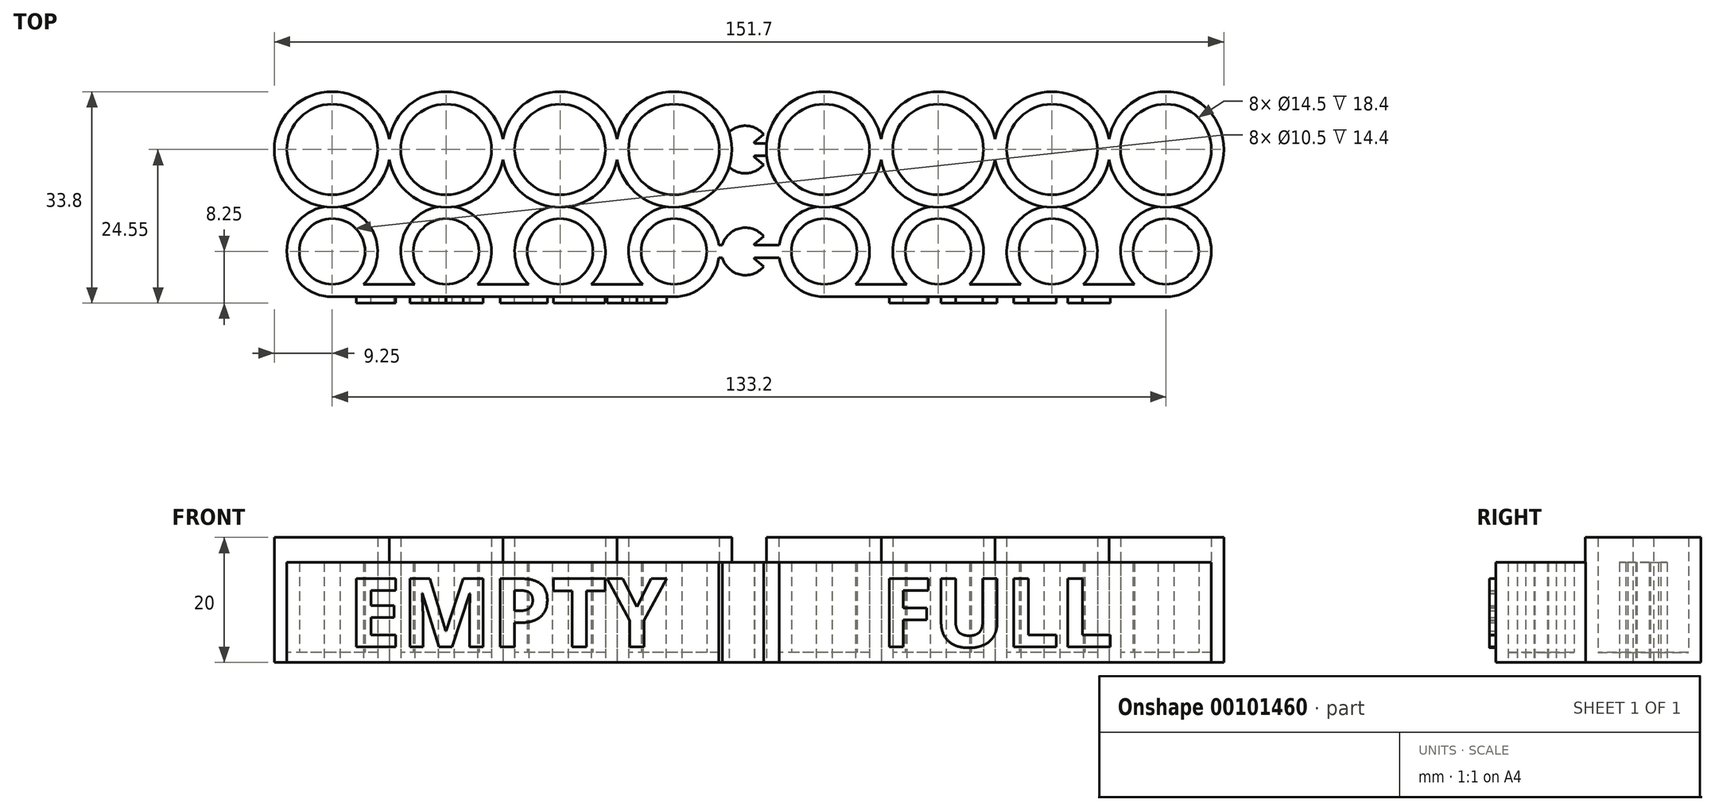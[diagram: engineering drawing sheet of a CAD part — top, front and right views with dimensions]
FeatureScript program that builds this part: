
annotation { "Feature Type Name" : "Feature", "Feature Type Description" : "" }
export const myFeature = defineFeature(function(context is Context, id is Id, definition is map)
    precondition{}
    {
        {
            var Q0;
            Q0=qCreatedBy(makeId("Top.planeOp"),FACE);
            var sketch = newSketch(context, id + "F0", { "sketchPlane" : qUnion([Q0])});
            skCircle(sketch, "E0", {"center": v(0, 0) * mm, "radius": 7.25 * mm});
            skCircle(sketch, "E1.0", {"center": v(0, 0) * mm, "radius": 9.25 * mm});
            skCircle(sketch, "E2.1.0.0", {"center": v(18.2, 0) * mm, "radius": 7.25 * mm});
            skCircle(sketch, "E2.1.0.1", {"center": v(18.2, 0) * mm, "radius": 9.25 * mm});
            skCircle(sketch, "E2.2.0.0", {"center": v(36.4, 0) * mm, "radius": 7.25 * mm});
            skCircle(sketch, "E2.2.0.1", {"center": v(36.4, 0) * mm, "radius": 9.25 * mm});
            skCircle(sketch, "E2.3.0.0", {"center": v(54.6, 0) * mm, "radius": 7.25 * mm});
            skCircle(sketch, "E2.3.0.1", {"center": v(54.6, 0) * mm, "radius": 9.25 * mm});
            skLineSegment(sketch, "E2.direction1", {"start": v(0, 0) * mm, "end": v(18.2, 0) * mm, "construction": true});
            skCircle(sketch, "E3", {"center": v(-24, 0) * mm, "radius": 7.25 * mm});
            skCircle(sketch, "E4.0", {"center": v(-24, 0) * mm, "radius": 9.25 * mm});
            skCircle(sketch, "E5.1.0.0", {"center": v(-42.2, 0) * mm, "radius": 9.25 * mm});
            skCircle(sketch, "E5.1.0.1", {"center": v(-42.2, 0) * mm, "radius": 7.25 * mm});
            skCircle(sketch, "E5.2.0.0", {"center": v(-60.4, 0) * mm, "radius": 9.25 * mm});
            skCircle(sketch, "E5.2.0.1", {"center": v(-60.4, 0) * mm, "radius": 7.25 * mm});
            skLineSegment(sketch, "E5.direction1", {"start": v(-24, 0) * mm, "end": v(-42.2, 0) * mm, "construction": true});
            skCircle(sketch, "E6.0.3.0", {"center": v(-78.6, 0) * mm, "radius": 9.25 * mm});
            skCircle(sketch, "E6.2.3.0", {"center": v(-78.6, 0) * mm, "radius": 7.25 * mm});
            skCircle(sketch, "E7", {"center": v(0, -16.3) * mm, "radius": 5.25 * mm});
            skCircle(sketch, "E8.0", {"center": v(0, -16.3) * mm, "radius": 7.25 * mm});
            skCircle(sketch, "E9.1.0.0", {"center": v(18.2, -16.3) * mm, "radius": 7.25 * mm});
            skCircle(sketch, "E9.1.0.1", {"center": v(18.2, -16.3) * mm, "radius": 5.25 * mm});
            skCircle(sketch, "E9.2.0.0", {"center": v(36.4, -16.3) * mm, "radius": 7.25 * mm});
            skCircle(sketch, "E9.2.0.1", {"center": v(36.4, -16.3) * mm, "radius": 5.25 * mm});
            skCircle(sketch, "E9.3.0.0", {"center": v(54.6, -16.3) * mm, "radius": 7.25 * mm});
            skCircle(sketch, "E9.3.0.1", {"center": v(54.6, -16.3) * mm, "radius": 5.25 * mm});
            skLineSegment(sketch, "E9.direction1", {"start": v(0, -16.3) * mm, "end": v(18.2, -16.3) * mm, "construction": true});
            skCircle(sketch, "E10", {"center": v(-24, -16.3) * mm, "radius": 5.25 * mm});
            skCircle(sketch, "E11.0", {"center": v(-24, -16.3) * mm, "radius": 7.25 * mm});
            skCircle(sketch, "E12.1.0.0", {"center": v(-42.2, -16.3) * mm, "radius": 7.25 * mm});
            skCircle(sketch, "E12.1.0.1", {"center": v(-42.2, -16.3) * mm, "radius": 5.25 * mm});
            skCircle(sketch, "E12.2.0.0", {"center": v(-60.4, -16.3) * mm, "radius": 7.25 * mm});
            skCircle(sketch, "E12.2.0.1", {"center": v(-60.4, -16.3) * mm, "radius": 5.25 * mm});
            skCircle(sketch, "E12.3.0.0", {"center": v(-78.6, -16.3) * mm, "radius": 7.25 * mm});
            skCircle(sketch, "E12.3.0.1", {"center": v(-78.6, -16.3) * mm, "radius": 5.25 * mm});
            skLineSegment(sketch, "E12.direction1", {"start": v(-24, -16.3) * mm, "end": v(-42.2, -16.3) * mm, "construction": true});
            skLineSegment(sketch, "E13", {"start": v(-9.2, 1) * mm, "end": v(-14.8, 1) * mm});
            skLineSegment(sketch, "E14.MirrorCS", {"start": v(-9.2, -1) * mm, "end": v(-14.8, -1) * mm});
            skLineSegment(sketch, "E15", {"start": v(-7.18, -15.3) * mm, "end": v(-16.82, -15.3) * mm});
            skLineSegment(sketch, "E16.MirrorCS", {"start": v(-7.18, -17.3) * mm, "end": v(-16.82, -17.3) * mm});
            skLineSegment(sketch, "E17", {"start": v(-78.6, -23.55) * mm, "end": v(-24, -23.55) * mm});
            skLineSegment(sketch, "E18", {"start": v(49.6, -21.55) * mm, "end": v(41.4, -21.55) * mm});
            skLineSegment(sketch, "E19.trimOffspring", {"start": v(0, -23.55) * mm, "end": v(54.6, -23.55) * mm});
            skPoint(sketch, "E20.orphan", {"position": v(-78.6, -21.55) * mm});
            skLineSegment(sketch, "E21.trimOffspring", {"start": v(-65.4, -21.55) * mm, "end": v(-73.6, -21.55) * mm});
            skLineSegment(sketch, "E22.trimOffspring", {"start": v(-47.2, -21.55) * mm, "end": v(-55.4, -21.55) * mm});
            skLineSegment(sketch, "E23.trimOffspring", {"start": v(-29, -21.55) * mm, "end": v(-37.2, -21.55) * mm});
            skLineSegment(sketch, "E24.trimOffspring", {"start": v(13.2, -21.55) * mm, "end": v(5, -21.55) * mm});
            skLineSegment(sketch, "E25.trimOffspring", {"start": v(31.4, -21.55) * mm, "end": v(23.2, -21.55) * mm});
            skPoint(sketch, "E26.orphan", {"position": v(54.6, -21.55) * mm});
            skCircle(sketch, "E27", {"center": v(-12.6, 0) * mm, "radius": 1.8 * mm});
            skCircle(sketch, "E28.0", {"center": v(-12.6, 0) * mm, "radius": 3.8 * mm});
            skLineSegment(sketch, "E29", {"start": v(-12.6, 0) * mm, "end": v(-9.69, 2.44) * mm});
            skLineSegment(sketch, "E30", {"start": v(-12.6, 0) * mm, "end": v(-9.69, -2.44) * mm});
            skCircle(sketch, "E31", {"center": v(-12.6, -16.3) * mm, "radius": 1.8 * mm});
            skCircle(sketch, "E32.0", {"center": v(-12.6, -16.3) * mm, "radius": 3.8 * mm});
            skLineSegment(sketch, "E33", {"start": v(-12.6, -16.3) * mm, "end": v(-9.69, -13.86) * mm});
            skLineSegment(sketch, "E34", {"start": v(-12.6, -16.3) * mm, "end": v(-9.69, -18.74) * mm});
            skSolve(sketch);
        }
        {
            var Q0;
            Q0=makeQuery(id+"F0.imprint","IMPRINT",FACE,{"disambiguationData":[TD([[makeQuery(id+"F0.imprint","IMPRINT",EDGE,{"derivedFrom":sQuery(id+"F0.wireOp",EDGE,"E6.2.3.0")}),-1.0]])]});
            var Q1;
            Q1=makeQuery(id+"F0.imprint","IMPRINT",FACE,{"disambiguationData":[TD([[makeQuery(id+"F0.imprint","IMPRINT",EDGE,{"derivedFrom":sQuery(id+"F0.wireOp",EDGE,"E5.2.0.1")}),-1.0]])]});
            var Q2;
            Q2=makeQuery(id+"F0.imprint","IMPRINT",FACE,{"disambiguationData":[TD([[makeQuery(id+"F0.imprint","IMPRINT",EDGE,{"derivedFrom":sQuery(id+"F0.wireOp",EDGE,"E5.1.0.1")}),-1.0]])]});
            var Q3;
            {var subQ3=sQuery(id+"F0.wireOp",EDGE,"E28.0");var subQ6=sQuery(id+"F0.wireOp",EDGE,"E3");var subQ7=makeQuery(id+"F0.imprint","INTERSECT",VERTEX,{"disambiguationData":[OD(0.0)],"derivedFrom":[subQ6,subQ3]});Q3=makeQuery(id+"F0.imprint","IMPRINT",FACE,{"disambiguationData":[TD([[makeQuery(id+"F0.imprint","IMPRINT",EDGE,{"disambiguationData":[TD([[subQ7,-1.0]])],"derivedFrom":subQ6}),-1.0]])]});}
            var Q4;
            {var subQ2=sQuery(id+"F0.wireOp",EDGE,"E28.0");var subQ9=sQuery(id+"F0.wireOp",EDGE,"E3");var subQ10=makeQuery(id+"F0.imprint","INTERSECT",VERTEX,{"disambiguationData":[OD(0.0)],"derivedFrom":[subQ9,subQ2]});Q4=makeQuery(id+"F0.imprint","IMPRINT",FACE,{"disambiguationData":[TD([[makeQuery(id+"F0.imprint","IMPRINT",EDGE,{"disambiguationData":[TD([[subQ10,1.0]])],"derivedFrom":subQ9}),-1.0]])]});}
            var Q5;
            {var subQ0=sQuery(id+"F0.wireOp",EDGE,"E6.0.3.0");var subQ1=sQuery(id+"F0.wireOp",EDGE,"E5.2.0.0");var subQ2=makeQuery(id+"F0.imprint","INTERSECT",VERTEX,{"disambiguationData":[OD(0.0)],"derivedFrom":[subQ1,subQ0]});Q5=makeQuery(id+"F0.imprint","IMPRINT",FACE,{"disambiguationData":[TD([[makeQuery(id+"F0.imprint","IMPRINT",EDGE,{"disambiguationData":[TD([[subQ2,-1.0]])],"derivedFrom":subQ1}),1.0]])]});}
            var Q6;
            {var subQ0=sQuery(id+"F0.wireOp",EDGE,"E5.2.0.0");var subQ1=sQuery(id+"F0.wireOp",EDGE,"E5.1.0.0");var subQ2=makeQuery(id+"F0.imprint","INTERSECT",VERTEX,{"disambiguationData":[OD(0.0)],"derivedFrom":[subQ1,subQ0]});Q6=makeQuery(id+"F0.imprint","IMPRINT",FACE,{"disambiguationData":[TD([[makeQuery(id+"F0.imprint","IMPRINT",EDGE,{"disambiguationData":[TD([[subQ2,-1.0]])],"derivedFrom":subQ1}),1.0]])]});}
            var Q7;
            {var subQ0=sQuery(id+"F0.wireOp",EDGE,"E5.1.0.0");var subQ1=sQuery(id+"F0.wireOp",EDGE,"E4.0");var subQ2=makeQuery(id+"F0.imprint","INTERSECT",VERTEX,{"disambiguationData":[OD(0.0)],"derivedFrom":[subQ1,subQ0]});Q7=makeQuery(id+"F0.imprint","IMPRINT",FACE,{"disambiguationData":[TD([[makeQuery(id+"F0.imprint","IMPRINT",EDGE,{"disambiguationData":[TD([[subQ2,-1.0]])],"derivedFrom":subQ1}),1.0]])]});}
            var Q8;
            {var subQ0=sQuery(id+"F0.wireOp",EDGE,"E11.0");var subQ1=sQuery(id+"F0.wireOp",EDGE,"E4.0");var subQ2=makeQuery(id+"F0.imprint","INTERSECT",VERTEX,{"disambiguationData":[OD(0.0)],"derivedFrom":[subQ1,subQ0]});Q8=makeQuery(id+"F0.imprint","IMPRINT",FACE,{"disambiguationData":[TD([[makeQuery(id+"F0.imprint","IMPRINT",EDGE,{"disambiguationData":[TD([[subQ2,-1.0]])],"derivedFrom":subQ1}),1.0]])]});}
            var Q9;
            {var subQ0=sQuery(id+"F0.wireOp",EDGE,"E12.1.0.0");var subQ1=sQuery(id+"F0.wireOp",EDGE,"E5.1.0.0");var subQ2=makeQuery(id+"F0.imprint","INTERSECT",VERTEX,{"disambiguationData":[OD(0.0)],"derivedFrom":[subQ1,subQ0]});Q9=makeQuery(id+"F0.imprint","IMPRINT",FACE,{"disambiguationData":[TD([[makeQuery(id+"F0.imprint","IMPRINT",EDGE,{"disambiguationData":[TD([[subQ2,-1.0]])],"derivedFrom":subQ1}),1.0]])]});}
            var Q10;
            {var subQ0=sQuery(id+"F0.wireOp",EDGE,"E12.2.0.0");var subQ1=sQuery(id+"F0.wireOp",EDGE,"E5.2.0.0");var subQ2=makeQuery(id+"F0.imprint","INTERSECT",VERTEX,{"disambiguationData":[OD(0.0)],"derivedFrom":[subQ1,subQ0]});Q10=makeQuery(id+"F0.imprint","IMPRINT",FACE,{"disambiguationData":[TD([[makeQuery(id+"F0.imprint","IMPRINT",EDGE,{"disambiguationData":[TD([[subQ2,-1.0]])],"derivedFrom":subQ1}),1.0]])]});}
            var Q11;
            {var subQ0=sQuery(id+"F0.wireOp",EDGE,"E12.3.0.0");var subQ1=sQuery(id+"F0.wireOp",EDGE,"E6.0.3.0");var subQ2=makeQuery(id+"F0.imprint","INTERSECT",VERTEX,{"disambiguationData":[OD(0.0)],"derivedFrom":[subQ1,subQ0]});Q11=makeQuery(id+"F0.imprint","IMPRINT",FACE,{"disambiguationData":[TD([[makeQuery(id+"F0.imprint","IMPRINT",EDGE,{"disambiguationData":[TD([[subQ2,-1.0]])],"derivedFrom":subQ1}),1.0]])]});}
            var Q12;
            {var subQ0=sQuery(id+"F0.wireOp",EDGE,"E27");var subQ1=sQuery(id+"F0.wireOp",EDGE,"E4.0");var subQ2=makeQuery(id+"F0.imprint","INTERSECT",VERTEX,{"disambiguationData":[OD(0.0)],"derivedFrom":[subQ1,subQ0]});Q12=makeQuery(id+"F0.imprint","IMPRINT",FACE,{"disambiguationData":[TD([[makeQuery(id+"F0.imprint","IMPRINT",EDGE,{"disambiguationData":[TD([[subQ2,1.0]])],"derivedFrom":subQ1}),1.0]])]});}
            var Q13;
            {var subQ0=sQuery(id+"F0.wireOp",EDGE,"E4.0");var subQ1=makeQuery(id+"F0.imprint","INTERSECT",VERTEX,{"derivedFrom":[subQ0,sQuery(id+"F0.wireOp",EDGE,"E13")]});Q13=makeQuery(id+"F0.imprint","IMPRINT",FACE,{"disambiguationData":[TD([[makeQuery(id+"F0.imprint","IMPRINT",EDGE,{"disambiguationData":[TD([[subQ1,-1.0]])],"derivedFrom":subQ0}),1.0]])]});}
            extrude(context, id + "F1", {"entities" : qUnion([Q0, Q1, Q2, Q3, Q4, Q5, Q6, Q7, Q8, Q9, Q10, Q11, Q12, Q13]), "depth" : 20 * mm});
        }
        {
            var Q0;
            {var subQ0=sQuery(id+"F0.wireOp",EDGE,"E15");var subQ1=sQuery(id+"F0.wireOp",EDGE,"E11.0");var subQ2=makeQuery(id+"F0.imprint","INTERSECT",VERTEX,{"derivedFrom":[subQ1,subQ0]});Q0=makeQuery(id+"F0.imprint","IMPRINT",FACE,{"disambiguationData":[TD([[makeQuery(id+"F0.imprint","IMPRINT",EDGE,{"disambiguationData":[TD([[subQ2,1.0]])],"derivedFrom":subQ1}),-1.0]])]});}
            var Q1;
            {var subQ0=sQuery(id+"F0.wireOp",EDGE,"E31");var subQ1=sQuery(id+"F0.wireOp",EDGE,"E15");var subQ2=makeQuery(id+"F0.imprint","INTERSECT",VERTEX,{"disambiguationData":[OD(1.0)],"derivedFrom":[subQ1,subQ0]});Q1=makeQuery(id+"F0.imprint","IMPRINT",FACE,{"disambiguationData":[TD([[makeQuery(id+"F0.imprint","IMPRINT",EDGE,{"disambiguationData":[TD([[subQ2,-1.0]])],"derivedFrom":subQ1}),1.0]])]});}
            var Q2;
            Q2=makeQuery(id+"F0.imprint","IMPRINT",FACE,{"disambiguationData":[TD([[makeQuery(id+"F0.imprint","IMPRINT",EDGE,{"derivedFrom":sQuery(id+"F0.wireOp",EDGE,"E12.3.0.1")}),-1.0]])]});
            var Q3;
            {var subQ0=sQuery(id+"F0.wireOp",EDGE,"E21.trimOffspring");Q3=makeQuery(id+"F0.imprint","IMPRINT",FACE,{"disambiguationData":[TD([[makeQuery(id+"F0.imprint","IMPRINT",EDGE,{"derivedFrom":subQ0}),1.0]])]});}
            var Q4;
            Q4=makeQuery(id+"F0.imprint","IMPRINT",FACE,{"disambiguationData":[TD([[makeQuery(id+"F0.imprint","IMPRINT",EDGE,{"derivedFrom":sQuery(id+"F0.wireOp",EDGE,"E12.2.0.1")}),-1.0]])]});
            var Q5;
            {var subQ0=sQuery(id+"F0.wireOp",EDGE,"E22.trimOffspring");Q5=makeQuery(id+"F0.imprint","IMPRINT",FACE,{"disambiguationData":[TD([[makeQuery(id+"F0.imprint","IMPRINT",EDGE,{"derivedFrom":subQ0}),1.0]])]});}
            var Q6;
            Q6=makeQuery(id+"F0.imprint","IMPRINT",FACE,{"disambiguationData":[TD([[makeQuery(id+"F0.imprint","IMPRINT",EDGE,{"derivedFrom":sQuery(id+"F0.wireOp",EDGE,"E12.1.0.1")}),-1.0]])]});
            var Q7;
            {var subQ3=sQuery(id+"F0.wireOp",EDGE,"E23.trimOffspring");Q7=makeQuery(id+"F0.imprint","IMPRINT",FACE,{"disambiguationData":[TD([[makeQuery(id+"F0.imprint","IMPRINT",EDGE,{"derivedFrom":subQ3}),1.0]])]});}
            var Q8;
            Q8=makeQuery(id+"F0.imprint","IMPRINT",FACE,{"disambiguationData":[TD([[makeQuery(id+"F0.imprint","IMPRINT",EDGE,{"derivedFrom":sQuery(id+"F0.wireOp",EDGE,"E10")}),-1.0]])]});
            var Q9;
            {var subQ3=sQuery(id+"F0.wireOp",EDGE,"E4.0");var subQ7=sQuery(id+"F0.wireOp",EDGE,"E13");var subQ9=makeQuery(id+"F0.imprint","INTERSECT",VERTEX,{"derivedFrom":[subQ3,subQ7]});Q9=makeQuery(id+"F0.imprint","IMPRINT",FACE,{"disambiguationData":[TD([[makeQuery(id+"F0.imprint","IMPRINT",EDGE,{"disambiguationData":[TD([[subQ9,-1.0]])],"derivedFrom":subQ3}),-1.0]])]});}
            var Q10;
            {var subQ0=sQuery(id+"F0.wireOp",EDGE,"E13");var subQ1=sQuery(id+"F0.wireOp",EDGE,"E4.0");var subQ2=makeQuery(id+"F0.imprint","INTERSECT",VERTEX,{"derivedFrom":[subQ1,subQ0]});Q10=makeQuery(id+"F0.imprint","IMPRINT",FACE,{"disambiguationData":[TD([[makeQuery(id+"F0.imprint","IMPRINT",EDGE,{"disambiguationData":[TD([[subQ2,1.0]])],"derivedFrom":subQ1}),-1.0]])]});}
            var Q11;
            {var subQ0=sQuery(id+"F0.wireOp",EDGE,"E13");var subQ1=sQuery(id+"F0.wireOp",EDGE,"E4.0");var subQ2=makeQuery(id+"F0.imprint","INTERSECT",VERTEX,{"derivedFrom":[subQ1,subQ0]});Q11=makeQuery(id+"F0.imprint","IMPRINT",FACE,{"disambiguationData":[TD([[makeQuery(id+"F0.imprint","IMPRINT",EDGE,{"disambiguationData":[TD([[subQ2,1.0]])],"derivedFrom":subQ1}),-1.0]])]});}
            var Q12;
            {var subQ3=sQuery(id+"F0.wireOp",EDGE,"E4.0");var subQ6=sQuery(id+"F0.wireOp",EDGE,"E14.MirrorCS");var subQ9=makeQuery(id+"F0.imprint","INTERSECT",VERTEX,{"derivedFrom":[subQ3,subQ6]});Q12=makeQuery(id+"F0.imprint","IMPRINT",FACE,{"disambiguationData":[TD([[makeQuery(id+"F0.imprint","IMPRINT",EDGE,{"disambiguationData":[TD([[subQ9,1.0]])],"derivedFrom":subQ3}),-1.0]])]});}
            var Q13;
            {var subQ0=sQuery(id+"F0.wireOp",EDGE,"E31");var subQ1=sQuery(id+"F0.wireOp",EDGE,"E15");var subQ2=makeQuery(id+"F0.imprint","INTERSECT",VERTEX,{"disambiguationData":[OD(1.0)],"derivedFrom":[subQ1,subQ0]});Q13=makeQuery(id+"F0.imprint","IMPRINT",FACE,{"disambiguationData":[TD([[makeQuery(id+"F0.imprint","IMPRINT",EDGE,{"disambiguationData":[TD([[subQ2,-1.0]])],"derivedFrom":subQ1}),-1.0]])]});}
            var Q14;
            {var subQ0=sQuery(id+"F0.wireOp",EDGE,"E15");var subQ1=sQuery(id+"F0.wireOp",EDGE,"E11.0");var subQ2=makeQuery(id+"F0.imprint","INTERSECT",VERTEX,{"derivedFrom":[subQ1,subQ0]});Q14=makeQuery(id+"F0.imprint","IMPRINT",FACE,{"disambiguationData":[TD([[makeQuery(id+"F0.imprint","IMPRINT",EDGE,{"disambiguationData":[TD([[subQ2,1.0]])],"derivedFrom":subQ1}),-1.0]])]});}
            var Q15;
            {var subQ0=sQuery(id+"F0.wireOp",EDGE,"E32.0");var subQ1=sQuery(id+"F0.wireOp",EDGE,"E16.MirrorCS");var subQ2=makeQuery(id+"F0.imprint","INTERSECT",VERTEX,{"disambiguationData":[OD(1.0)],"derivedFrom":[subQ1,subQ0]});Q15=makeQuery(id+"F0.imprint","IMPRINT",FACE,{"disambiguationData":[TD([[makeQuery(id+"F0.imprint","IMPRINT",EDGE,{"disambiguationData":[TD([[subQ2,1.0]])],"derivedFrom":subQ1}),1.0]])]});}
            var Q16;
            Q16=makeQuery(id+"F0.imprint","IMPRINT",FACE,{"disambiguationData":[TD([[makeQuery(id+"F0.imprint","IMPRINT",EDGE,{"derivedFrom":sQuery(id+"F0.wireOp",EDGE,"E10")}),-1.0]])]});
            extrude(context, id + "F2", {"entities" : qUnion([Q0, Q1, Q2, Q3, Q4, Q5, Q6, Q7, Q8, Q9, Q10, Q11, Q12, Q13, Q14, Q15, Q16]), "operationType" : NewBodyOperationType.ADD, "depth" : 16 * mm});
        }
        {
            var Q0;
            Q0=makeQuery(id+"F0.imprint","IMPRINT",FACE,{"disambiguationData":[TD([[makeQuery(id+"F0.imprint","IMPRINT",EDGE,{"derivedFrom":sQuery(id+"F0.wireOp",EDGE,"E5.1.0.1")}),1.0]])]});
            var Q1;
            Q1=makeQuery(id+"F0.imprint","IMPRINT",FACE,{"disambiguationData":[TD([[makeQuery(id+"F0.imprint","IMPRINT",EDGE,{"derivedFrom":sQuery(id+"F0.wireOp",EDGE,"E3")}),1.0]])]});
            var Q2;
            Q2=makeQuery(id+"F0.imprint","IMPRINT",FACE,{"disambiguationData":[TD([[makeQuery(id+"F0.imprint","IMPRINT",EDGE,{"derivedFrom":sQuery(id+"F0.wireOp",EDGE,"E5.2.0.1")}),1.0]])]});
            var Q3;
            Q3=makeQuery(id+"F0.imprint","IMPRINT",FACE,{"disambiguationData":[TD([[makeQuery(id+"F0.imprint","IMPRINT",EDGE,{"derivedFrom":sQuery(id+"F0.wireOp",EDGE,"E6.2.3.0")}),1.0]])]});
            var Q4;
            Q4=makeQuery(id+"F0.imprint","IMPRINT",FACE,{"disambiguationData":[TD([[makeQuery(id+"F0.imprint","IMPRINT",EDGE,{"derivedFrom":sQuery(id+"F0.wireOp",EDGE,"E10")}),1.0]])]});
            var Q5;
            Q5=makeQuery(id+"F0.imprint","IMPRINT",FACE,{"disambiguationData":[TD([[makeQuery(id+"F0.imprint","IMPRINT",EDGE,{"derivedFrom":sQuery(id+"F0.wireOp",EDGE,"E12.1.0.1")}),1.0]])]});
            var Q6;
            Q6=makeQuery(id+"F0.imprint","IMPRINT",FACE,{"disambiguationData":[TD([[makeQuery(id+"F0.imprint","IMPRINT",EDGE,{"derivedFrom":sQuery(id+"F0.wireOp",EDGE,"E12.2.0.1")}),1.0]])]});
            var Q7;
            Q7=makeQuery(id+"F0.imprint","IMPRINT",FACE,{"disambiguationData":[TD([[makeQuery(id+"F0.imprint","IMPRINT",EDGE,{"derivedFrom":sQuery(id+"F0.wireOp",EDGE,"E12.3.0.1")}),1.0]])]});
            extrude(context, id + "F3", {"entities" : qUnion([Q0, Q1, Q2, Q3, Q4, Q5, Q6, Q7]), "operationType" : NewBodyOperationType.ADD, "depth" : 1.6 * mm});
        }
        {
            var Q0;
            Q0=makeQuery(id+"F2.opExtrude","SWEPT_FACE",FACE,{"disambiguationData":[OSD([sQuery(id+"F0.wireOp",EDGE,"E17")])]});
            var sketch = newSketch(context, id + "F4", { "sketchPlane" : qUnion([Q0])});
            skText(sketch, "E35", { "text": "EMPTY", "fontName": "OpenSans-Bold.ttf"});
            const initialGuessF4  = {"E35": [-0.0761, 0.0025, 1, 0, 0.011]};
            skSetInitialGuess(sketch, initialGuessF4);
            skSolve(sketch);
        }
        {
            var Q0;
            Q0=makeQuery(id+"F4.imprint","IMPRINT",FACE,{"disambiguationData":[TD([[makeQuery(id+"F4.imprint","IMPRINT",EDGE,{"derivedFrom":sQuery(id+"F4.wireOp",EDGE,"E35.sketch_text.stroke-0")}),-1.0]])]});
            var Q1;
            Q1=makeQuery(id+"F4.imprint","IMPRINT",FACE,{"disambiguationData":[TD([[makeQuery(id+"F4.imprint","IMPRINT",EDGE,{"derivedFrom":sQuery(id+"F4.wireOp",EDGE,"E35.sketch_text.stroke-12")}),-1.0]])]});
            var Q2;
            Q2=makeQuery(id+"F4.imprint","IMPRINT",FACE,{"disambiguationData":[TD([[makeQuery(id+"F4.imprint","IMPRINT",EDGE,{"derivedFrom":sQuery(id+"F4.wireOp",EDGE,"E35.sketch_text.stroke-31")}),-1.0]])]});
            var Q3;
            Q3=makeQuery(id+"F4.imprint","IMPRINT",FACE,{"disambiguationData":[TD([[makeQuery(id+"F4.imprint","IMPRINT",EDGE,{"derivedFrom":sQuery(id+"F4.wireOp",EDGE,"E35.sketch_text.stroke-47")}),-1.0]])]});
            var Q4;
            Q4=makeQuery(id+"F4.imprint","IMPRINT",FACE,{"disambiguationData":[TD([[makeQuery(id+"F4.imprint","IMPRINT",EDGE,{"derivedFrom":sQuery(id+"F4.wireOp",EDGE,"E35.sketch_text.stroke-55")}),-1.0]])]});
            extrude(context, id + "F5", {"entities" : qUnion([Q0, Q1, Q2, Q3, Q4]), "operationType" : NewBodyOperationType.ADD, "depth" : 1 * mm});
        }
        {
            var Q0;
            Q0=makeQuery(id+"F0.imprint","IMPRINT",FACE,{"disambiguationData":[TD([[makeQuery(id+"F0.imprint","IMPRINT",EDGE,{"derivedFrom":sQuery(id+"F0.wireOp",EDGE,"E0")}),-1.0]])]});
            var Q1;
            {var subQ0=sQuery(id+"F0.wireOp",EDGE,"E1.0");var subQ1=makeQuery(id+"F0.imprint","INTERSECT",VERTEX,{"derivedFrom":[subQ0,sQuery(id+"F0.wireOp",EDGE,"E13")]});Q1=makeQuery(id+"F0.imprint","IMPRINT",FACE,{"disambiguationData":[TD([[makeQuery(id+"F0.imprint","IMPRINT",EDGE,{"disambiguationData":[TD([[subQ1,1.0]])],"derivedFrom":subQ0}),1.0]])]});}
            var Q2;
            {var subQ0=sQuery(id+"F0.wireOp",EDGE,"E2.1.0.1");var subQ1=sQuery(id+"F0.wireOp",EDGE,"E1.0");var subQ2=makeQuery(id+"F0.imprint","INTERSECT",VERTEX,{"disambiguationData":[OD(0.0)],"derivedFrom":[subQ1,subQ0]});Q2=makeQuery(id+"F0.imprint","IMPRINT",FACE,{"disambiguationData":[TD([[makeQuery(id+"F0.imprint","IMPRINT",EDGE,{"disambiguationData":[TD([[subQ2,1.0]])],"derivedFrom":subQ1}),1.0]])]});}
            var Q3;
            Q3=makeQuery(id+"F0.imprint","IMPRINT",FACE,{"disambiguationData":[TD([[makeQuery(id+"F0.imprint","IMPRINT",EDGE,{"derivedFrom":sQuery(id+"F0.wireOp",EDGE,"E2.1.0.0")}),-1.0]])]});
            var Q4;
            {var subQ0=sQuery(id+"F0.wireOp",EDGE,"E2.2.0.1");var subQ1=sQuery(id+"F0.wireOp",EDGE,"E2.1.0.1");var subQ2=makeQuery(id+"F0.imprint","INTERSECT",VERTEX,{"disambiguationData":[OD(0.0)],"derivedFrom":[subQ1,subQ0]});Q4=makeQuery(id+"F0.imprint","IMPRINT",FACE,{"disambiguationData":[TD([[makeQuery(id+"F0.imprint","IMPRINT",EDGE,{"disambiguationData":[TD([[subQ2,1.0]])],"derivedFrom":subQ1}),1.0]])]});}
            var Q5;
            Q5=makeQuery(id+"F0.imprint","IMPRINT",FACE,{"disambiguationData":[TD([[makeQuery(id+"F0.imprint","IMPRINT",EDGE,{"derivedFrom":sQuery(id+"F0.wireOp",EDGE,"E2.2.0.0")}),-1.0]])]});
            var Q6;
            {var subQ0=sQuery(id+"F0.wireOp",EDGE,"E2.3.0.1");var subQ1=sQuery(id+"F0.wireOp",EDGE,"E2.2.0.1");var subQ2=makeQuery(id+"F0.imprint","INTERSECT",VERTEX,{"disambiguationData":[OD(0.0)],"derivedFrom":[subQ1,subQ0]});Q6=makeQuery(id+"F0.imprint","IMPRINT",FACE,{"disambiguationData":[TD([[makeQuery(id+"F0.imprint","IMPRINT",EDGE,{"disambiguationData":[TD([[subQ2,1.0]])],"derivedFrom":subQ1}),1.0]])]});}
            var Q7;
            Q7=makeQuery(id+"F0.imprint","IMPRINT",FACE,{"disambiguationData":[TD([[makeQuery(id+"F0.imprint","IMPRINT",EDGE,{"derivedFrom":sQuery(id+"F0.wireOp",EDGE,"E2.3.0.0")}),-1.0]])]});
            var Q8;
            {var subQ0=sQuery(id+"F0.wireOp",EDGE,"E8.0");var subQ1=sQuery(id+"F0.wireOp",EDGE,"E1.0");var subQ2=makeQuery(id+"F0.imprint","INTERSECT",VERTEX,{"disambiguationData":[OD(0.0)],"derivedFrom":[subQ1,subQ0]});Q8=makeQuery(id+"F0.imprint","IMPRINT",FACE,{"disambiguationData":[TD([[makeQuery(id+"F0.imprint","IMPRINT",EDGE,{"disambiguationData":[TD([[subQ2,-1.0]])],"derivedFrom":subQ1}),1.0]])]});}
            var Q9;
            {var subQ0=sQuery(id+"F0.wireOp",EDGE,"E9.1.0.0");var subQ1=sQuery(id+"F0.wireOp",EDGE,"E2.1.0.1");var subQ2=makeQuery(id+"F0.imprint","INTERSECT",VERTEX,{"disambiguationData":[OD(0.0)],"derivedFrom":[subQ1,subQ0]});Q9=makeQuery(id+"F0.imprint","IMPRINT",FACE,{"disambiguationData":[TD([[makeQuery(id+"F0.imprint","IMPRINT",EDGE,{"disambiguationData":[TD([[subQ2,-1.0]])],"derivedFrom":subQ1}),1.0]])]});}
            var Q10;
            {var subQ0=sQuery(id+"F0.wireOp",EDGE,"E9.2.0.0");var subQ1=sQuery(id+"F0.wireOp",EDGE,"E2.2.0.1");var subQ2=makeQuery(id+"F0.imprint","INTERSECT",VERTEX,{"disambiguationData":[OD(0.0)],"derivedFrom":[subQ1,subQ0]});Q10=makeQuery(id+"F0.imprint","IMPRINT",FACE,{"disambiguationData":[TD([[makeQuery(id+"F0.imprint","IMPRINT",EDGE,{"disambiguationData":[TD([[subQ2,-1.0]])],"derivedFrom":subQ1}),1.0]])]});}
            var Q11;
            {var subQ0=sQuery(id+"F0.wireOp",EDGE,"E9.3.0.0");var subQ1=sQuery(id+"F0.wireOp",EDGE,"E2.3.0.1");var subQ2=makeQuery(id+"F0.imprint","INTERSECT",VERTEX,{"disambiguationData":[OD(0.0)],"derivedFrom":[subQ1,subQ0]});Q11=makeQuery(id+"F0.imprint","IMPRINT",FACE,{"disambiguationData":[TD([[makeQuery(id+"F0.imprint","IMPRINT",EDGE,{"disambiguationData":[TD([[subQ2,1.0]])],"derivedFrom":subQ1}),1.0]])]});}
            extrude(context, id + "F6", {"entities" : qUnion([Q0, Q1, Q2, Q3, Q4, Q5, Q6, Q7, Q8, Q9, Q10, Q11]), "depth" : 20 * mm});
        }
        {
            var Q0;
            {var subQ0=sQuery(id+"F0.wireOp",EDGE,"E29");var subQ1=sQuery(id+"F0.wireOp",EDGE,"E13");var subQ2=makeQuery(id+"F0.imprint","INTERSECT",VERTEX,{"derivedFrom":[subQ1,subQ0]});Q0=makeQuery(id+"F0.imprint","IMPRINT",FACE,{"disambiguationData":[TD([[makeQuery(id+"F0.imprint","IMPRINT",EDGE,{"disambiguationData":[TD([[subQ2,-1.0]])],"derivedFrom":subQ1}),-1.0]])]});}
            var Q1;
            {var subQ1=sQuery(id+"F0.wireOp",EDGE,"E29");var subQ3=sQuery(id+"F0.wireOp",EDGE,"E13");var subQ4=makeQuery(id+"F0.imprint","INTERSECT",VERTEX,{"derivedFrom":[subQ3,subQ1]});Q1=makeQuery(id+"F0.imprint","IMPRINT",FACE,{"disambiguationData":[TD([[makeQuery(id+"F0.imprint","IMPRINT",EDGE,{"disambiguationData":[TD([[subQ4,-1.0]])],"derivedFrom":subQ3}),1.0]])]});}
            var Q2;
            {var subQ0=sQuery(id+"F0.wireOp",EDGE,"E30");var subQ1=sQuery(id+"F0.wireOp",EDGE,"E14.MirrorCS");var subQ2=makeQuery(id+"F0.imprint","INTERSECT",VERTEX,{"derivedFrom":[subQ1,subQ0]});Q2=makeQuery(id+"F0.imprint","IMPRINT",FACE,{"disambiguationData":[TD([[makeQuery(id+"F0.imprint","IMPRINT",EDGE,{"disambiguationData":[TD([[subQ2,-1.0]])],"derivedFrom":subQ1}),1.0]])]});}
            var Q3;
            {var subQ3=sQuery(id+"F0.wireOp",EDGE,"E13");var subQ5=sQuery(id+"F0.wireOp",EDGE,"E27");var subQ6=makeQuery(id+"F0.imprint","INTERSECT",VERTEX,{"disambiguationData":[OD(0.0)],"derivedFrom":[subQ3,subQ5]});Q3=makeQuery(id+"F0.imprint","IMPRINT",FACE,{"disambiguationData":[TD([[makeQuery(id+"F0.imprint","IMPRINT",EDGE,{"disambiguationData":[TD([[subQ6,-1.0]])],"derivedFrom":subQ3}),1.0]])]});}
            var Q4;
            {var subQ0=sQuery(id+"F0.wireOp",EDGE,"E27");var subQ1=sQuery(id+"F0.wireOp",EDGE,"E13");var subQ2=makeQuery(id+"F0.imprint","INTERSECT",VERTEX,{"disambiguationData":[OD(0.0)],"derivedFrom":[subQ1,subQ0]});Q4=makeQuery(id+"F0.imprint","IMPRINT",FACE,{"disambiguationData":[TD([[makeQuery(id+"F0.imprint","IMPRINT",EDGE,{"disambiguationData":[TD([[subQ2,-1.0]])],"derivedFrom":subQ1}),-1.0]])]});}
            var Q5;
            {var subQ0=sQuery(id+"F0.wireOp",EDGE,"E27");var subQ1=sQuery(id+"F0.wireOp",EDGE,"E14.MirrorCS");var subQ2=makeQuery(id+"F0.imprint","INTERSECT",VERTEX,{"disambiguationData":[OD(0.0)],"derivedFrom":[subQ1,subQ0]});Q5=makeQuery(id+"F0.imprint","IMPRINT",FACE,{"disambiguationData":[TD([[makeQuery(id+"F0.imprint","IMPRINT",EDGE,{"disambiguationData":[TD([[subQ2,-1.0]])],"derivedFrom":subQ1}),1.0]])]});}
            var Q6;
            {var subQ0=sQuery(id+"F0.wireOp",EDGE,"E13");var subQ1=sQuery(id+"F0.wireOp",EDGE,"E1.0");var subQ2=makeQuery(id+"F0.imprint","INTERSECT",VERTEX,{"derivedFrom":[subQ1,subQ0]});Q6=makeQuery(id+"F0.imprint","IMPRINT",FACE,{"disambiguationData":[TD([[makeQuery(id+"F0.imprint","IMPRINT",EDGE,{"disambiguationData":[TD([[subQ2,-1.0]])],"derivedFrom":subQ1}),-1.0]])]});}
            var Q7;
            {var subQ0=sQuery(id+"F0.wireOp",EDGE,"E33");var subQ1=sQuery(id+"F0.wireOp",EDGE,"E15");var subQ2=makeQuery(id+"F0.imprint","INTERSECT",VERTEX,{"derivedFrom":[subQ1,subQ0]});Q7=makeQuery(id+"F0.imprint","IMPRINT",FACE,{"disambiguationData":[TD([[makeQuery(id+"F0.imprint","IMPRINT",EDGE,{"disambiguationData":[TD([[subQ2,-1.0]])],"derivedFrom":subQ1}),-1.0]])]});}
            var Q8;
            {var subQ1=sQuery(id+"F0.wireOp",EDGE,"E33");var subQ3=sQuery(id+"F0.wireOp",EDGE,"E15");var subQ4=makeQuery(id+"F0.imprint","INTERSECT",VERTEX,{"derivedFrom":[subQ3,subQ1]});Q8=makeQuery(id+"F0.imprint","IMPRINT",FACE,{"disambiguationData":[TD([[makeQuery(id+"F0.imprint","IMPRINT",EDGE,{"disambiguationData":[TD([[subQ4,-1.0]])],"derivedFrom":subQ3}),1.0]])]});}
            var Q9;
            {var subQ0=sQuery(id+"F0.wireOp",EDGE,"E34");var subQ1=sQuery(id+"F0.wireOp",EDGE,"E16.MirrorCS");var subQ2=makeQuery(id+"F0.imprint","INTERSECT",VERTEX,{"derivedFrom":[subQ1,subQ0]});Q9=makeQuery(id+"F0.imprint","IMPRINT",FACE,{"disambiguationData":[TD([[makeQuery(id+"F0.imprint","IMPRINT",EDGE,{"disambiguationData":[TD([[subQ2,-1.0]])],"derivedFrom":subQ1}),1.0]])]});}
            var Q10;
            {var subQ0=sQuery(id+"F0.wireOp",EDGE,"E31");var subQ1=sQuery(id+"F0.wireOp",EDGE,"E16.MirrorCS");var subQ2=makeQuery(id+"F0.imprint","INTERSECT",VERTEX,{"disambiguationData":[OD(0.0)],"derivedFrom":[subQ1,subQ0]});Q10=makeQuery(id+"F0.imprint","IMPRINT",FACE,{"disambiguationData":[TD([[makeQuery(id+"F0.imprint","IMPRINT",EDGE,{"disambiguationData":[TD([[subQ2,-1.0]])],"derivedFrom":subQ1}),1.0]])]});}
            var Q11;
            {var subQ0=sQuery(id+"F0.wireOp",EDGE,"E31");var subQ1=sQuery(id+"F0.wireOp",EDGE,"E15");var subQ2=makeQuery(id+"F0.imprint","INTERSECT",VERTEX,{"disambiguationData":[OD(0.0)],"derivedFrom":[subQ1,subQ0]});Q11=makeQuery(id+"F0.imprint","IMPRINT",FACE,{"disambiguationData":[TD([[makeQuery(id+"F0.imprint","IMPRINT",EDGE,{"disambiguationData":[TD([[subQ2,-1.0]])],"derivedFrom":subQ1}),1.0]])]});}
            var Q12;
            {var subQ0=sQuery(id+"F0.wireOp",EDGE,"E31");var subQ1=sQuery(id+"F0.wireOp",EDGE,"E15");var subQ2=makeQuery(id+"F0.imprint","INTERSECT",VERTEX,{"disambiguationData":[OD(0.0)],"derivedFrom":[subQ1,subQ0]});Q12=makeQuery(id+"F0.imprint","IMPRINT",FACE,{"disambiguationData":[TD([[makeQuery(id+"F0.imprint","IMPRINT",EDGE,{"disambiguationData":[TD([[subQ2,-1.0]])],"derivedFrom":subQ1}),-1.0]])]});}
            var Q13;
            {var subQ0=sQuery(id+"F0.wireOp",EDGE,"E32.0");var subQ1=sQuery(id+"F0.wireOp",EDGE,"E15");var subQ2=makeQuery(id+"F0.imprint","INTERSECT",VERTEX,{"disambiguationData":[OD(0.0)],"derivedFrom":[subQ1,subQ0]});Q13=makeQuery(id+"F0.imprint","IMPRINT",FACE,{"disambiguationData":[TD([[makeQuery(id+"F0.imprint","IMPRINT",EDGE,{"disambiguationData":[TD([[subQ2,-1.0]])],"derivedFrom":subQ1}),1.0]])]});}
            var Q14;
            {var subQ0=sQuery(id+"F0.wireOp",EDGE,"E15");var subQ1=sQuery(id+"F0.wireOp",EDGE,"E8.0");var subQ2=makeQuery(id+"F0.imprint","INTERSECT",VERTEX,{"derivedFrom":[subQ1,subQ0]});Q14=makeQuery(id+"F0.imprint","IMPRINT",FACE,{"disambiguationData":[TD([[makeQuery(id+"F0.imprint","IMPRINT",EDGE,{"disambiguationData":[TD([[subQ2,-1.0]])],"derivedFrom":subQ1}),-1.0]])]});}
            var Q15;
            Q15=makeQuery(id+"F0.imprint","IMPRINT",FACE,{"disambiguationData":[TD([[makeQuery(id+"F0.imprint","IMPRINT",EDGE,{"derivedFrom":sQuery(id+"F0.wireOp",EDGE,"E7")}),-1.0]])]});
            var Q16;
            {var subQ3=sQuery(id+"F0.wireOp",EDGE,"E24.trimOffspring");Q16=makeQuery(id+"F0.imprint","IMPRINT",FACE,{"disambiguationData":[TD([[makeQuery(id+"F0.imprint","IMPRINT",EDGE,{"derivedFrom":subQ3}),1.0]])]});}
            var Q17;
            Q17=makeQuery(id+"F0.imprint","IMPRINT",FACE,{"disambiguationData":[TD([[makeQuery(id+"F0.imprint","IMPRINT",EDGE,{"derivedFrom":sQuery(id+"F0.wireOp",EDGE,"E9.1.0.1")}),-1.0]])]});
            var Q18;
            {var subQ0=sQuery(id+"F0.wireOp",EDGE,"E25.trimOffspring");Q18=makeQuery(id+"F0.imprint","IMPRINT",FACE,{"disambiguationData":[TD([[makeQuery(id+"F0.imprint","IMPRINT",EDGE,{"derivedFrom":subQ0}),1.0]])]});}
            var Q19;
            Q19=makeQuery(id+"F0.imprint","IMPRINT",FACE,{"disambiguationData":[TD([[makeQuery(id+"F0.imprint","IMPRINT",EDGE,{"derivedFrom":sQuery(id+"F0.wireOp",EDGE,"E9.2.0.1")}),-1.0]])]});
            var Q20;
            {var subQ0=sQuery(id+"F0.wireOp",EDGE,"E18");Q20=makeQuery(id+"F0.imprint","IMPRINT",FACE,{"disambiguationData":[TD([[makeQuery(id+"F0.imprint","IMPRINT",EDGE,{"derivedFrom":subQ0}),1.0]])]});}
            var Q21;
            Q21=makeQuery(id+"F0.imprint","IMPRINT",FACE,{"disambiguationData":[TD([[makeQuery(id+"F0.imprint","IMPRINT",EDGE,{"derivedFrom":sQuery(id+"F0.wireOp",EDGE,"E9.3.0.1")}),-1.0]])]});
            extrude(context, id + "F7", {"entities" : qUnion([Q0, Q1, Q2, Q3, Q4, Q5, Q6, Q7, Q8, Q9, Q10, Q11, Q12, Q13, Q14, Q15, Q16, Q17, Q18, Q19, Q20, Q21]), "operationType" : NewBodyOperationType.ADD, "depth" : 16 * mm});
        }
        {
            var Q0;
            Q0=makeQuery(id+"F7.opExtrude","SWEPT_FACE",FACE,{"disambiguationData":[OSD([sQuery(id+"F0.wireOp",EDGE,"E19.trimOffspring")])]});
            var sketch = newSketch(context, id + "F8", { "sketchPlane" : qUnion([Q0])});
            skText(sketch, "E36", { "text": "FULL", "fontName": "OpenSans-Bold.ttf"});
            const initialGuessF8  = {"E36": [0.009, 0.0025, 1, 0, 0.011]};
            skSetInitialGuess(sketch, initialGuessF8);
            skSolve(sketch);
        }
        {
            var Q0;
            Q0=makeQuery(id+"F8.imprint","IMPRINT",FACE,{"disambiguationData":[TD([[makeQuery(id+"F8.imprint","IMPRINT",EDGE,{"derivedFrom":sQuery(id+"F8.wireOp",EDGE,"E36.sketch_text.stroke-0")}),-1.0]])]});
            var Q1;
            Q1=makeQuery(id+"F8.imprint","IMPRINT",FACE,{"disambiguationData":[TD([[makeQuery(id+"F8.imprint","IMPRINT",EDGE,{"derivedFrom":sQuery(id+"F8.wireOp",EDGE,"E36.sketch_text.stroke-10")}),-1.0]])]});
            var Q2;
            Q2=makeQuery(id+"F8.imprint","IMPRINT",FACE,{"disambiguationData":[TD([[makeQuery(id+"F8.imprint","IMPRINT",EDGE,{"derivedFrom":sQuery(id+"F8.wireOp",EDGE,"E36.sketch_text.stroke-25")}),-1.0]])]});
            var Q3;
            Q3=makeQuery(id+"F8.imprint","IMPRINT",FACE,{"disambiguationData":[TD([[makeQuery(id+"F8.imprint","IMPRINT",EDGE,{"derivedFrom":sQuery(id+"F8.wireOp",EDGE,"E36.sketch_text.stroke-31")}),-1.0]])]});
            extrude(context, id + "F9", {"entities" : qUnion([Q0, Q1, Q2, Q3]), "operationType" : NewBodyOperationType.ADD, "depth" : 1 * mm});
        }
        {
            var Q0;
            Q0=makeQuery(id+"F0.imprint","IMPRINT",FACE,{"disambiguationData":[TD([[makeQuery(id+"F0.imprint","IMPRINT",EDGE,{"derivedFrom":sQuery(id+"F0.wireOp",EDGE,"E0")}),1.0]])]});
            var Q1;
            Q1=makeQuery(id+"F0.imprint","IMPRINT",FACE,{"disambiguationData":[TD([[makeQuery(id+"F0.imprint","IMPRINT",EDGE,{"derivedFrom":sQuery(id+"F0.wireOp",EDGE,"E2.1.0.0")}),1.0]])]});
            var Q2;
            Q2=makeQuery(id+"F0.imprint","IMPRINT",FACE,{"disambiguationData":[TD([[makeQuery(id+"F0.imprint","IMPRINT",EDGE,{"derivedFrom":sQuery(id+"F0.wireOp",EDGE,"E2.2.0.0")}),1.0]])]});
            var Q3;
            Q3=makeQuery(id+"F0.imprint","IMPRINT",FACE,{"disambiguationData":[TD([[makeQuery(id+"F0.imprint","IMPRINT",EDGE,{"derivedFrom":sQuery(id+"F0.wireOp",EDGE,"E2.3.0.0")}),1.0]])]});
            var Q4;
            Q4=makeQuery(id+"F0.imprint","IMPRINT",FACE,{"disambiguationData":[TD([[makeQuery(id+"F0.imprint","IMPRINT",EDGE,{"derivedFrom":sQuery(id+"F0.wireOp",EDGE,"E9.3.0.1")}),1.0]])]});
            var Q5;
            Q5=makeQuery(id+"F0.imprint","IMPRINT",FACE,{"disambiguationData":[TD([[makeQuery(id+"F0.imprint","IMPRINT",EDGE,{"derivedFrom":sQuery(id+"F0.wireOp",EDGE,"E9.2.0.1")}),1.0]])]});
            var Q6;
            Q6=makeQuery(id+"F0.imprint","IMPRINT",FACE,{"disambiguationData":[TD([[makeQuery(id+"F0.imprint","IMPRINT",EDGE,{"derivedFrom":sQuery(id+"F0.wireOp",EDGE,"E9.1.0.1")}),1.0]])]});
            var Q7;
            Q7=makeQuery(id+"F0.imprint","IMPRINT",FACE,{"disambiguationData":[TD([[makeQuery(id+"F0.imprint","IMPRINT",EDGE,{"derivedFrom":sQuery(id+"F0.wireOp",EDGE,"E7")}),1.0]])]});
            extrude(context, id + "F10", {"entities" : qUnion([Q0, Q1, Q2, Q3, Q4, Q5, Q6, Q7]), "operationType" : NewBodyOperationType.ADD, "depth" : 1.6 * mm});
        }
    });
